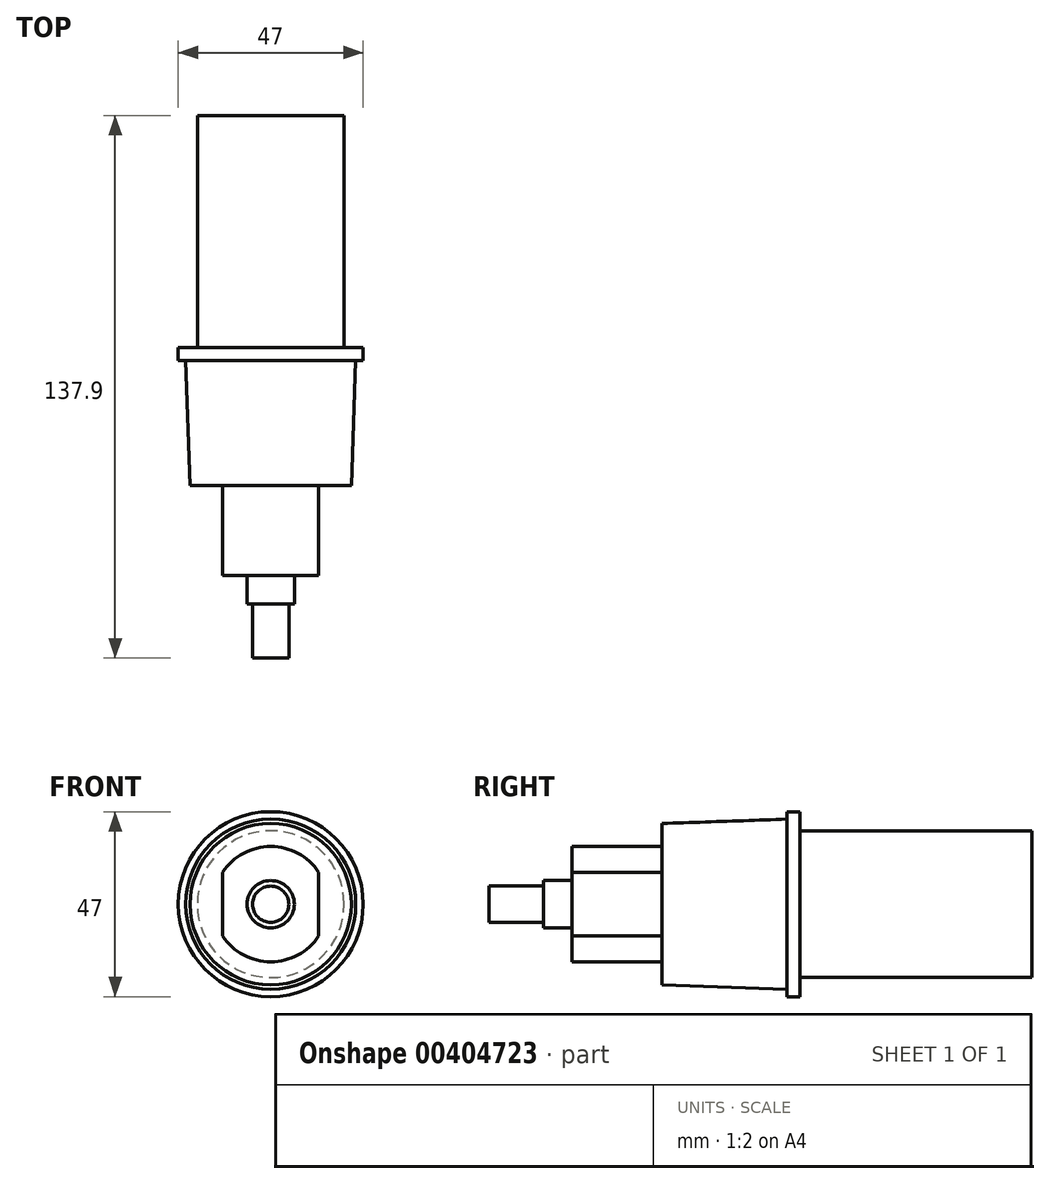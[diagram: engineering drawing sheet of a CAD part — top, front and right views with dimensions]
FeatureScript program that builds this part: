
annotation { "Feature Type Name" : "Feature", "Feature Type Description" : "" }
export const myFeature = defineFeature(function(context is Context, id is Id, definition is map)
    precondition{}
    {
        {
            var Q0;
            Q0=qCreatedBy(makeId("Front.planeOp"),FACE);
            var sketch = newSketch(context, id + "F0", { "sketchPlane" : qUnion([Q0])});
            skCircle(sketch, "E0", {"center": v(0, 0) * mm, "radius": 18.65 * mm});
            skSolve(sketch);
        }
        {
            var Q0;
            Q0=makeQuery(id+"F0.imprint","IMPRINT",FACE,{"disambiguationData":[TD([[makeQuery(id+"F0.imprint","IMPRINT",EDGE,{"derivedFrom":sQuery(id+"F0.wireOp",EDGE,"E0")}),1.0]])]});
            extrude(context, id + "F1", {"entities" : qUnion([Q0]), "oppositeDirection" : true, "depth" : 59 * mm});
        }
        {
            var Q0;
            Q0=qCreatedBy(makeId("Top.planeOp"),FACE);
            var sketch = newSketch(context, id + "F2", { "sketchPlane" : qUnion([Q0])});
            skLineSegment(sketch, "E1", {"start": v(0, 0) * mm, "end": v(0, -35) * mm});
            skLineSegment(sketch, "E2", {"start": v(0, -35) * mm, "end": v(20.5, -35) * mm});
            skLineSegment(sketch, "E3", {"start": v(20.5, -35) * mm, "end": v(21.6, -3.3) * mm});
            skLineSegment(sketch, "E4", {"start": v(21.6, -3.3) * mm, "end": v(23.5, -3.3) * mm});
            skLineSegment(sketch, "E5", {"start": v(23.5, -3.3) * mm, "end": v(23.5, 0) * mm});
            skLineSegment(sketch, "E6", {"start": v(23.5, 0) * mm, "end": v(0, 0) * mm});
            skSolve(sketch);
        }
        {
            var Q0;
            Q0 = qSketchRegion(id + "F2", true);
            var Q1;
            Q1=sQuery(id+"F2.wireOp",EDGE,"E1");
            revolve(context, id + "F3", {"operationType" : NewBodyOperationType.ADD, "entities" : qUnion([Q0]), "axis" : qUnion([Q1]), "revolveType" : RevolveType.FULL});
        }
        {
            var Q0;
            Q0=makeQuery(id+"F3.opRevolve","SWEPT_FACE",FACE,{"disambiguationData":[OSD([sQuery(id+"F2.wireOp",EDGE,"E2")])]});
            var sketch = newSketch(context, id + "F4", { "sketchPlane" : qUnion([Q0])});
            skCircle(sketch, "E7", {"center": v(0, 0) * mm, "radius": 6 * mm});
            skLineSegment(sketch, "E8", {"start": v(-12.2, 8.11) * mm, "end": v(-12.2, -8.11) * mm});
            skLineSegment(sketch, "E9", {"start": v(12.2, 8.11) * mm, "end": v(12.2, -8.11) * mm});
            skCircle(sketch, "E10", {"center": v(0, 0) * mm, "radius": 14.65 * mm});
            skCircle(sketch, "E11", {"center": v(0, 0) * mm, "radius": 4.6 * mm});
            skSolve(sketch);
        }
        {
            var Q0;
            Q0=makeQuery(id+"F4.imprint","IMPRINT",FACE,{"disambiguationData":[TD([[makeQuery(id+"F4.imprint","IMPRINT",EDGE,{"derivedFrom":sQuery(id+"F4.wireOp",EDGE,"E7")}),-1.0]])]});
            var Q1;
            Q1=makeQuery(id+"F4.imprint","IMPRINT",FACE,{"disambiguationData":[TD([[makeQuery(id+"F4.imprint","IMPRINT",EDGE,{"derivedFrom":sQuery(id+"F4.wireOp",EDGE,"E7")}),1.0]])]});
            var Q2;
            Q2=makeQuery(id+"F4.imprint","IMPRINT",FACE,{"disambiguationData":[TD([[makeQuery(id+"F4.imprint","IMPRINT",EDGE,{"derivedFrom":sQuery(id+"F4.wireOp",EDGE,"E11")}),1.0]])]});
            extrude(context, id + "F5", {"entities" : qUnion([Q0, Q1, Q2]), "operationType" : NewBodyOperationType.ADD, "depth" : 22.9 * mm});
        }
        {
            var Q0;
            Q0=makeQuery(id+"F4.imprint","IMPRINT",FACE,{"disambiguationData":[TD([[makeQuery(id+"F4.imprint","IMPRINT",EDGE,{"derivedFrom":sQuery(id+"F4.wireOp",EDGE,"E7")}),1.0]])]});
            var Q1;
            Q1=makeQuery(id+"F4.imprint","IMPRINT",FACE,{"disambiguationData":[TD([[makeQuery(id+"F4.imprint","IMPRINT",EDGE,{"derivedFrom":sQuery(id+"F4.wireOp",EDGE,"E11")}),1.0]])]});
            extrude(context, id + "F6", {"entities" : qUnion([Q0, Q1]), "operationType" : NewBodyOperationType.ADD, "depth" : 30.1 * mm});
        }
        {
            var Q0;
            Q0=makeQuery(id+"F4.imprint","IMPRINT",FACE,{"disambiguationData":[TD([[makeQuery(id+"F4.imprint","IMPRINT",EDGE,{"derivedFrom":sQuery(id+"F4.wireOp",EDGE,"E11")}),1.0]])]});
            extrude(context, id + "F7", {"entities" : qUnion([Q0]), "operationType" : NewBodyOperationType.ADD, "depth" : 43.9 * mm});
        }
    });
